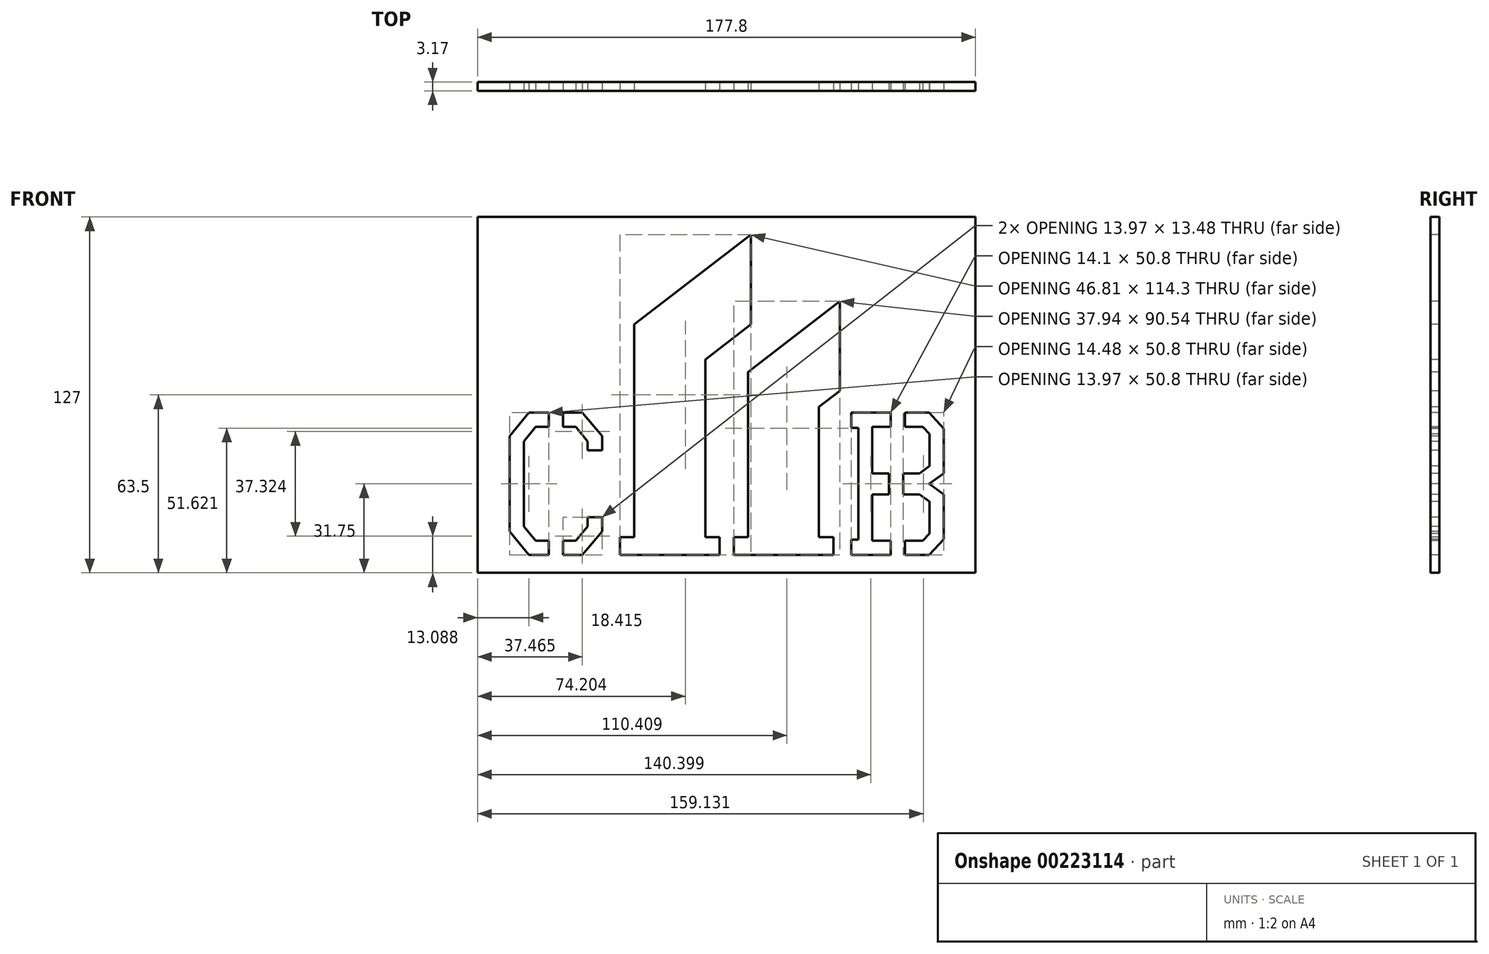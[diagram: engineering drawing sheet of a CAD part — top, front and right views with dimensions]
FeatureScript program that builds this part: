
annotation { "Feature Type Name" : "Feature", "Feature Type Description" : "" }
export const myFeature = defineFeature(function(context is Context, id is Id, definition is map)
    precondition{}
    {
        {
            var Q0;
            Q0=qCreatedBy(makeId("Front.planeOp"),FACE);
            var sketch = newSketch(context, id + "F0", { "sketchPlane" : qUnion([Q0])});
            skLineSegment(sketch, "E0.bottom", {"start": v(88.9, -63.5) * mm, "end": v(-88.9, -63.5) * mm});
            skLineSegment(sketch, "E0.top", {"start": v(88.9, 63.5) * mm, "end": v(-88.9, 63.5) * mm});
            skLineSegment(sketch, "E0.left", {"start": v(88.9, -63.5) * mm, "end": v(88.9, 63.5) * mm});
            skLineSegment(sketch, "E0.right", {"start": v(-88.9, -63.5) * mm, "end": v(-88.9, 63.5) * mm});
            skPoint(sketch, "E0.middle", {"position": v(0, 0) * mm});
            skSolve(sketch);
        }
        {
            var Q0;
            Q0 = qSketchRegion(id + "F0", true);
            extrude(context, id + "F1", {"entities" : qUnion([Q0]), "oppositeDirection" : true, "depth" : 3.17 * mm});
        }
        {
            var Q0;
            Q0=makeQuery(id+"F1.opExtrude","CAP_FACE",FACE,{"disambiguationData":[OSD([sQuery(id+"F0.wireOp",EDGE,"E0.bottom"),sQuery(id+"F0.wireOp",EDGE,"E0.top"),sQuery(id+"F0.wireOp",EDGE,"E0.left"),sQuery(id+"F0.wireOp",EDGE,"E0.right")])],"isStart":true});
            var sketch = newSketch(context, id + "F2", { "sketchPlane" : qUnion([Q0])});
            skLineSegment(sketch, "E1", {"start": v(-38.1, -57.15) * mm, "end": v(-2.54, -57.15) * mm});
            skLineSegment(sketch, "E2", {"start": v(-7.62, -50.8) * mm, "end": v(-7.62, 12.63) * mm});
            skLineSegment(sketch, "E3", {"start": v(-7.62, 12.63) * mm, "end": v(8.7, 25.15) * mm});
            skLineSegment(sketch, "E4", {"start": v(8.7, 57.15) * mm, "end": v(-33.02, 25.16) * mm});
            skLineSegment(sketch, "E5", {"start": v(-33.02, 25.16) * mm, "end": v(-33.02, -50.8) * mm});
            skLineSegment(sketch, "E6", {"start": v(8.7, 25.15) * mm, "end": v(8.7, 57.15) * mm});
            skLineSegment(sketch, "E7", {"start": v(38.1, -57.15) * mm, "end": v(38.1, -50.8) * mm});
            skLineSegment(sketch, "E8", {"start": v(38.1, -50.8) * mm, "end": v(2.54, -50.8) * mm});
            skLineSegment(sketch, "E9", {"start": v(-38.1, -50.8) * mm, "end": v(-38.1, -57.15) * mm});
            skLineSegment(sketch, "E10", {"start": v(0, -63.5) * mm, "end": v(0, -57.15) * mm, "construction": true});
            skLineSegment(sketch, "E11", {"start": v(-48.23, 0) * mm, "end": v(49.94, 0) * mm, "construction": true});
            skLineSegment(sketch, "E12", {"start": v(88.9, 0) * mm, "end": v(49.94, 0) * mm, "construction": true});
            skLineSegment(sketch, "E13", {"start": v(0, -57.15) * mm, "end": v(0, -46.15) * mm, "construction": true});
            skPoint(sketch, "E13.endSnap0", {"position": v(0, -50.8) * mm});
            skLineSegment(sketch, "E14", {"start": v(7.62, -50.8) * mm, "end": v(7.62, 8.2) * mm});
            skLineSegment(sketch, "E15", {"start": v(7.62, 8.2) * mm, "end": v(40.48, 33.4) * mm});
            skLineSegment(sketch, "E16", {"start": v(40.48, 1.39) * mm, "end": v(33.02, -4.33) * mm});
            skLineSegment(sketch, "E17", {"start": v(33.02, -4.33) * mm, "end": v(33.02, -50.8) * mm});
            skLineSegment(sketch, "E18", {"start": v(40.48, 1.39) * mm, "end": v(40.48, 33.4) * mm});
            skLineSegment(sketch, "E19", {"start": v(0, -50.8) * mm, "end": v(0, -67.2) * mm, "construction": true});
            skLineSegment(sketch, "E20", {"start": v(-2.54, -50.8) * mm, "end": v(-2.54, -57.15) * mm});
            skLineSegment(sketch, "E21.MirrorCS", {"start": v(2.54, -50.8) * mm, "end": v(2.54, -57.15) * mm});
            skLineSegment(sketch, "E22.trimOffspring", {"start": v(2.54, -57.15) * mm, "end": v(38.1, -57.15) * mm});
            skLineSegment(sketch, "E23.trimOffspring", {"start": v(-2.54, -50.8) * mm, "end": v(-38.1, -50.8) * mm});
            skSolve(sketch);
        }
        {
            var Q0;
            Q0 = qSketchRegion(id + "F2", true);
            var Q1;
            {var subQ0=sQuery(id+"F0.wireOp",EDGE,"E0.right");var subQ1=sQuery(id+"F0.wireOp",EDGE,"E0.left");var subQ2=sQuery(id+"F0.wireOp",EDGE,"E0.top");var subQ3=sQuery(id+"F0.wireOp",EDGE,"E0.bottom");Q1=makeQuery(id+"FnrUEDNc1CUpauk_1.boolean.opBoolean","SPLIT",FACE,{"disambiguationData":[TD([makeQuery(id+"F1.opExtrude","SWEPT_FACE",FACE,{"disambiguationData":[OSD([subQ3])]})])],"derivedFrom":makeQuery(id+"F1.opExtrude","CAP_FACE",FACE,{"disambiguationData":[OSD([subQ3,subQ2,subQ1,subQ0])],"isStart":false})});}
            extrude(context, id + "F3", {"entities" : qUnion([Q0]), "operationType" : NewBodyOperationType.REMOVE, "endBound" : BoundingType.UP_TO_SURFACE, "oppositeDirection" : true, "endBoundEntityFace" : qUnion([Q1]), "depth" : 25.4 * mm});
        }
        {
            var Q0;
            Q0=makeQuery(id+"F1.opExtrude","CAP_FACE",FACE,{"disambiguationData":[OSD([sQuery(id+"F0.wireOp",EDGE,"E0.bottom"),sQuery(id+"F0.wireOp",EDGE,"E0.top"),sQuery(id+"F0.wireOp",EDGE,"E0.left"),sQuery(id+"F0.wireOp",EDGE,"E0.right")])],"isStart":true});
            var sketch = newSketch(context, id + "F4", { "sketchPlane" : qUnion([Q0])});
            skLineSegment(sketch, "E24", {"start": v(-77.47, -31.75) * mm, "end": v(-77.47, -14.75) * mm});
            skLineSegment(sketch, "E25", {"start": v(-77.47, -14.75) * mm, "end": v(-70.48, -6.35) * mm});
            skLineSegment(sketch, "E26", {"start": v(-70.48, -6.35) * mm, "end": v(-63.5, -6.35) * mm});
            skLineSegment(sketch, "E27", {"start": v(-51.43, -6.35) * mm, "end": v(-44.45, -14.75) * mm});
            skLineSegment(sketch, "E28", {"start": v(-44.45, -14.75) * mm, "end": v(-44.45, -19.83) * mm});
            skLineSegment(sketch, "E29", {"start": v(-77.47, -31.75) * mm, "end": v(-62.18, -31.75) * mm, "construction": true});
            skLineSegment(sketch, "E30.MirrorCS", {"start": v(-77.47, -31.75) * mm, "end": v(-77.47, -48.75) * mm});
            skLineSegment(sketch, "E31.MirrorCS", {"start": v(-77.47, -48.75) * mm, "end": v(-70.48, -57.15) * mm});
            skLineSegment(sketch, "E32.MirrorCS", {"start": v(-70.48, -57.15) * mm, "end": v(-63.5, -57.15) * mm});
            skLineSegment(sketch, "E33.MirrorCS", {"start": v(-51.43, -57.15) * mm, "end": v(-44.45, -48.75) * mm});
            skLineSegment(sketch, "E34.MirrorCS", {"start": v(-44.45, -48.75) * mm, "end": v(-44.45, -43.67) * mm});
            skLineSegment(sketch, "E35.0", {"start": v(-49.53, -16.58) * mm, "end": v(-49.53, -19.83) * mm});
            skLineSegment(sketch, "E35.1", {"start": v(-53.82, -11.43) * mm, "end": v(-49.53, -16.58) * mm});
            skLineSegment(sketch, "E35.2", {"start": v(-68.1, -11.43) * mm, "end": v(-63.5, -11.43) * mm});
            skLineSegment(sketch, "E35.3", {"start": v(-72.39, -16.58) * mm, "end": v(-68.1, -11.43) * mm});
            skLineSegment(sketch, "E35.4", {"start": v(-72.39, -31.75) * mm, "end": v(-72.39, -16.58) * mm});
            skLineSegment(sketch, "E35.5", {"start": v(-72.39, -31.75) * mm, "end": v(-72.39, -46.92) * mm});
            skLineSegment(sketch, "E35.6", {"start": v(-49.53, -46.92) * mm, "end": v(-49.53, -43.67) * mm});
            skLineSegment(sketch, "E35.7", {"start": v(-53.82, -52.07) * mm, "end": v(-49.53, -46.92) * mm});
            skLineSegment(sketch, "E35.8", {"start": v(-68.1, -52.07) * mm, "end": v(-63.5, -52.07) * mm});
            skLineSegment(sketch, "E35.9", {"start": v(-72.4, -46.92) * mm, "end": v(-68.1, -52.07) * mm});
            skLineSegment(sketch, "E36", {"start": v(-49.53, -19.83) * mm, "end": v(-44.45, -19.83) * mm});
            skLineSegment(sketch, "E37", {"start": v(-49.53, -43.67) * mm, "end": v(-44.45, -43.67) * mm});
            skLineSegment(sketch, "E38", {"start": v(-38.1, -57.15) * mm, "end": v(-58.42, -57.15) * mm, "construction": true});
            skLineSegment(sketch, "E39", {"start": v(-38.1, -57.15) * mm, "end": v(94.87, -57.15) * mm, "construction": true});
            skLineSegment(sketch, "E40", {"start": v(44.45, -6.35) * mm, "end": v(44.45, -11.81) * mm});
            skLineSegment(sketch, "E41", {"start": v(44.45, -11.81) * mm, "end": v(46.99, -11.81) * mm});
            skLineSegment(sketch, "E42", {"start": v(46.99, -11.81) * mm, "end": v(46.99, -31.75) * mm});
            skLineSegment(sketch, "E43", {"start": v(46.99, -31.75) * mm, "end": v(76.89, -31.75) * mm, "construction": true});
            skLineSegment(sketch, "E44", {"start": v(44.45, -6.35) * mm, "end": v(58.55, -6.35) * mm});
            skLineSegment(sketch, "E45", {"start": v(72.36, -6.35) * mm, "end": v(77.47, -12) * mm});
            skLineSegment(sketch, "E46", {"start": v(77.47, -12) * mm, "end": v(77.47, -28) * mm});
            skLineSegment(sketch, "E47", {"start": v(77.47, -28) * mm, "end": v(72.34, -31.75) * mm});
            skLineSegment(sketch, "E48.MirrorCS", {"start": v(77.47, -35.5) * mm, "end": v(72.34, -31.75) * mm});
            skLineSegment(sketch, "E49.MirrorCS", {"start": v(77.47, -51.5) * mm, "end": v(77.47, -35.5) * mm});
            skLineSegment(sketch, "E50.MirrorCS", {"start": v(72.36, -57.15) * mm, "end": v(77.47, -51.5) * mm});
            skLineSegment(sketch, "E51.MirrorCS", {"start": v(44.45, -57.15) * mm, "end": v(58.55, -57.15) * mm});
            skLineSegment(sketch, "E52.MirrorCS", {"start": v(44.45, -57.15) * mm, "end": v(44.45, -51.69) * mm});
            skLineSegment(sketch, "E53.MirrorCS", {"start": v(44.45, -51.69) * mm, "end": v(46.99, -51.69) * mm});
            skLineSegment(sketch, "E54.MirrorCS", {"start": v(46.99, -51.69) * mm, "end": v(46.99, -31.75) * mm});
            skLineSegment(sketch, "E55.0", {"start": v(52.07, -11.43) * mm, "end": v(52.07, -28.02) * mm});
            skLineSegment(sketch, "E55.1", {"start": v(52.07, -52.07) * mm, "end": v(52.07, -35.48) * mm});
            skLineSegment(sketch, "E55.2", {"start": v(52.07, -11.43) * mm, "end": v(58.55, -11.43) * mm});
            skLineSegment(sketch, "E55.3", {"start": v(52.07, -52.07) * mm, "end": v(58.55, -52.07) * mm});
            skLineSegment(sketch, "E55.4", {"start": v(70.1, -52.07) * mm, "end": v(72.39, -49.54) * mm});
            skLineSegment(sketch, "E55.5", {"start": v(72.39, -49.54) * mm, "end": v(72.39, -38.08) * mm});
            skLineSegment(sketch, "E55.6", {"start": v(70.1, -11.43) * mm, "end": v(72.39, -13.96) * mm});
            skLineSegment(sketch, "E55.7", {"start": v(72.39, -13.96) * mm, "end": v(72.39, -25.42) * mm});
            skLineSegment(sketch, "E55.8", {"start": v(72.39, -25.42) * mm, "end": v(68.83, -28.02) * mm});
            skLineSegment(sketch, "E55.9", {"start": v(72.4, -38.08) * mm, "end": v(68.83, -35.48) * mm});
            skLineSegment(sketch, "E56", {"start": v(52.07, -28.02) * mm, "end": v(57.91, -28.02) * mm});
            skLineSegment(sketch, "E57.MirrorCS", {"start": v(52.07, -35.48) * mm, "end": v(57.91, -35.48) * mm});
            skLineSegment(sketch, "E58", {"start": v(61.09, -11.43) * mm, "end": v(61.09, -3.33) * mm, "construction": true});
            skLineSegment(sketch, "E59", {"start": v(58.55, -11.43) * mm, "end": v(58.55, -6.35) * mm});
            skLineSegment(sketch, "E60.MirrorCS", {"start": v(63.63, -11.43) * mm, "end": v(63.63, -6.35) * mm});
            skLineSegment(sketch, "E61.trimOffspring", {"start": v(63.63, -6.35) * mm, "end": v(72.36, -6.35) * mm});
            skLineSegment(sketch, "E62.trimOffspring", {"start": v(63.63, -11.43) * mm, "end": v(70.1, -11.43) * mm});
            skLineSegment(sketch, "E63.MirrorCS", {"start": v(63.63, -52.07) * mm, "end": v(63.63, -57.15) * mm});
            skLineSegment(sketch, "E64.MirrorCS", {"start": v(58.55, -52.07) * mm, "end": v(58.55, -57.15) * mm});
            skLineSegment(sketch, "E65.trimOffspring", {"start": v(63.63, -52.07) * mm, "end": v(70.1, -52.07) * mm});
            skLineSegment(sketch, "E66.trimOffspring", {"start": v(63.63, -57.15) * mm, "end": v(72.36, -57.15) * mm});
            skLineSegment(sketch, "E67", {"start": v(-60.96, -11.43) * mm, "end": v(-60.96, -2.66) * mm, "construction": true});
            skLineSegment(sketch, "E68", {"start": v(-63.5, -11.43) * mm, "end": v(-63.5, -6.35) * mm});
            skLineSegment(sketch, "E69.MirrorCS", {"start": v(-58.42, -11.43) * mm, "end": v(-58.42, -6.35) * mm});
            skLineSegment(sketch, "E70.trimOffspring", {"start": v(-58.42, -6.35) * mm, "end": v(-51.43, -6.35) * mm});
            skLineSegment(sketch, "E71.trimOffspring", {"start": v(-58.42, -11.43) * mm, "end": v(-53.82, -11.43) * mm});
            skLineSegment(sketch, "E72.MirrorCS", {"start": v(-58.42, -52.07) * mm, "end": v(-58.42, -57.15) * mm});
            skLineSegment(sketch, "E73.MirrorCS", {"start": v(-63.5, -52.07) * mm, "end": v(-63.5, -57.15) * mm});
            skLineSegment(sketch, "E74.trimOffspring", {"start": v(-58.42, -52.07) * mm, "end": v(-53.82, -52.07) * mm});
            skLineSegment(sketch, "E75.trimOffspring", {"start": v(-63.5, -57.15) * mm, "end": v(-98.17, -57.15) * mm, "construction": true});
            skLineSegment(sketch, "E76.trimOffspring", {"start": v(-58.42, -57.15) * mm, "end": v(-51.43, -57.15) * mm});
            skLineSegment(sketch, "E77", {"start": v(60.45, -35.48) * mm, "end": v(60.45, -24.78) * mm, "construction": true});
            skPoint(sketch, "E77.endSnap0", {"position": v(60.45, -28.02) * mm});
            skLineSegment(sketch, "E78", {"start": v(57.91, -35.48) * mm, "end": v(57.91, -28.02) * mm});
            skLineSegment(sketch, "E79.MirrorCS", {"start": v(63, -35.48) * mm, "end": v(63, -28.02) * mm});
            skLineSegment(sketch, "E80.trimOffspring", {"start": v(63, -28.02) * mm, "end": v(68.83, -28.02) * mm});
            skLineSegment(sketch, "E81.trimOffspring", {"start": v(63, -35.48) * mm, "end": v(68.83, -35.48) * mm});
            skSolve(sketch);
        }
        {
            var Q0;
            Q0 = qSketchRegion(id + "F4", true);
            var Q1;
            Q1=makeQuery(id+"F1.opExtrude","CAP_FACE",FACE,{"disambiguationData":[OSD([sQuery(id+"F0.wireOp",EDGE,"E0.bottom"),sQuery(id+"F0.wireOp",EDGE,"E0.top"),sQuery(id+"F0.wireOp",EDGE,"E0.left"),sQuery(id+"F0.wireOp",EDGE,"E0.right")])],"isStart":false});
            extrude(context, id + "F5", {"entities" : qUnion([Q0]), "operationType" : NewBodyOperationType.REMOVE, "endBound" : BoundingType.UP_TO_SURFACE, "oppositeDirection" : true, "endBoundEntityFace" : qUnion([Q1]), "depth" : 25.4 * mm});
        }
    });
